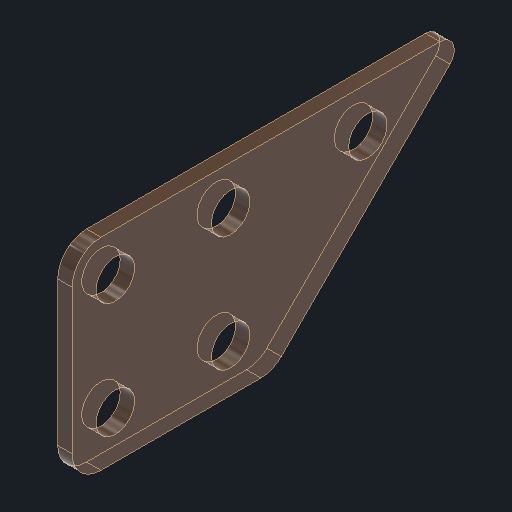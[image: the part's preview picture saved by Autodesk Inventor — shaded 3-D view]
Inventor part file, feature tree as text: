
AUTODESK INVENTOR PART (.ipt)
format: ipt  version: 2024 (Build 280153000, 153)  size: 129,536 bytes
history: native  units: in
note: dims shown in document units (in); Inventor stores cm internally (conversion verified against a paired STEP export)
features: other x3, sketch x3
ambient origin geometry x8: Origin, YZ Plane, XZ Plane, XY Plane, X Axis, Y Axis, Z Axis, Center Point
bodies: Solid1 (feature_tree)
feature tree (6):
  other  "sled-old.ipt"
  other  "Solid1::sled-old.ipt"
  other  "TaggingFeature1"
  sketch  "Sketch1"  dims[d0=0.3937in]
  sketch  "Sketch2"
  sketch  "Sketch3"
